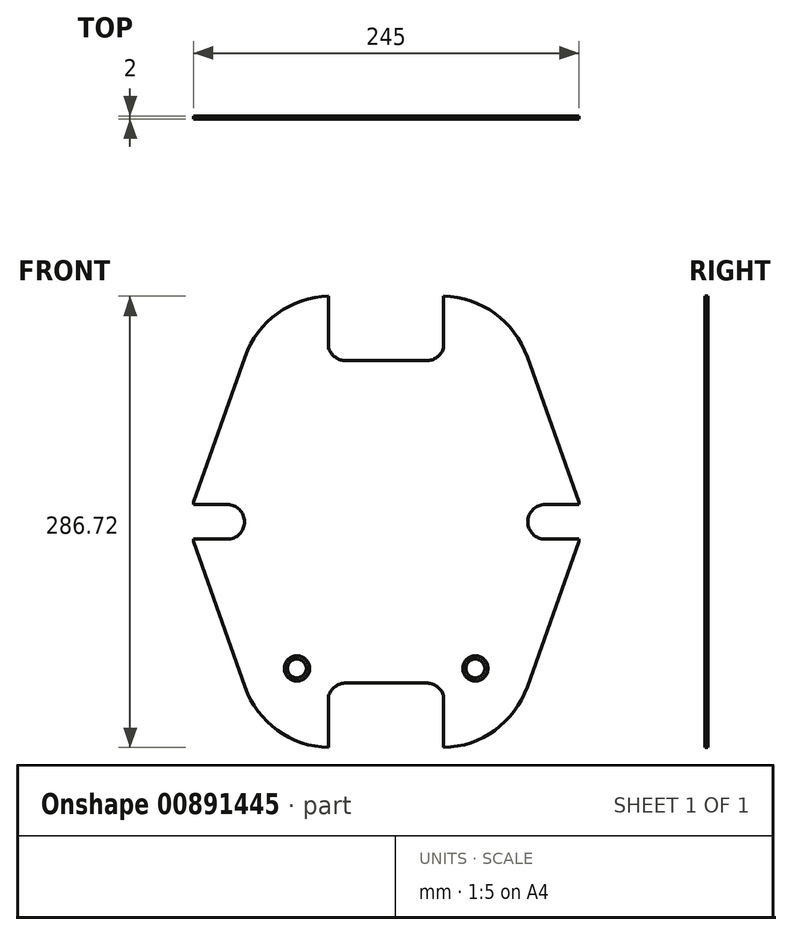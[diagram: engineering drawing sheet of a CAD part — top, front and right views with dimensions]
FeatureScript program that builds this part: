
annotation { "Feature Type Name" : "Feature", "Feature Type Description" : "" }
export const myFeature = defineFeature(function(context is Context, id is Id, definition is map)
    precondition{}
    {
        {
            var Q0;
            Q0=qCreatedBy(makeId("Front.planeOp"),FACE);
            var sketch = newSketch(context, id + "F0", { "sketchPlane" : qUnion([Q0])});
            skLineSegment(sketch, "E0", {"start": v(-122.5, 130.86) * mm, "end": v(122.5, 130.86) * mm});
            skLineSegment(sketch, "E1", {"start": v(122.5, 130.86) * mm, "end": v(89.64, 38.53) * mm});
            skLineSegment(sketch, "E2", {"start": v(-122.5, 130.86) * mm, "end": v(-89.64, 38.53) * mm});
            skArc(sketch, "E3", {"start": v(-89.64, 38.53) * mm, "mid": v(-69.05, 11.03) * mm, "end": v(-36.5, 0) * mm});
            skArc(sketch, "E4", {"start": v(36.5, 0) * mm, "mid": v(69.05, 11.03) * mm, "end": v(89.64, 38.53) * mm});
            skLineSegment(sketch, "E5", {"start": v(-36.5, 0) * mm, "end": v(-36.5, 33) * mm});
            skLineSegment(sketch, "E6", {"start": v(-36.5, 33) * mm, "end": v(36.5, 33) * mm, "construction": true});
            skLineSegment(sketch, "E7", {"start": v(36.5, 33) * mm, "end": v(36.5, 0) * mm});
            skLineSegment(sketch, "E8", {"start": v(0, 33) * mm, "end": v(0, 0) * mm, "construction": true});
            skLineSegment(sketch, "E9", {"start": v(-25.5, 41) * mm, "end": v(25.5, 41) * mm});
            skArc(sketch, "E10", {"start": v(-25.5, 41) * mm, "mid": v(-32.3, 38.79) * mm, "end": v(-36.5, 33) * mm});
            skArc(sketch, "E11", {"start": v(36.5, 33) * mm, "mid": v(32.3, 38.79) * mm, "end": v(25.5, 41) * mm});
            skPoint(sketch, "E12", {"position": v(-56.67, 50.27) * mm});
            skLineSegment(sketch, "E13", {"start": v(-89.64, 38.53) * mm, "end": v(-56.67, 50.27) * mm, "construction": true});
            skPoint(sketch, "E14", {"position": v(56.67, 50.27) * mm});
            skSolve(sketch);
        }
        {
            var Q0;
            Q0=qSketchRegion(id+"F0",true);
            extrude(context, id + "F1", {"entities" : qUnion([Q0]), "oppositeDirection" : true, "depth" : 2 * mm, "offsetDistance" : 25 * mm});
        }
        {
            var Q0;
            Q0=makeQuery(id+"F1.opExtrude","SWEPT_FACE",FACE,{"disambiguationData":[OSD([sQuery(id+"F0.wireOp",EDGE,"E0")])]});
            cPlane(context, id + "F2", {"entities" : qUnion([Q0]), "cplaneType" : CPlaneType.OFFSET, "offset" : 12.5 * mm, "width" : 150 * mm, "height" : 150 * mm});
        }
        {
            var Q0;
            Q0=makeQuery(id+"F1.opExtrude","SWEPT_BODY",BODY,{"disambiguationData":[OSD([sQuery(id+"F0.wireOp",EDGE,"E0"),sQuery(id+"F0.wireOp",EDGE,"E1"),sQuery(id+"F0.wireOp",EDGE,"E2"),sQuery(id+"F0.wireOp",EDGE,"E3"),sQuery(id+"F0.wireOp",EDGE,"RBLw4Hvx-HNYR-cSoG-CBft-1KmUEeb84xH9"),sQuery(id+"F0.wireOp",EDGE,"E4")])]});
            var Q1;
            Q1=qCreatedBy(id+"F2.planeOp",FACE);
            mirror(context, id + "F3", {"entities" : qUnion([Q0]), "mirrorPlane" : qUnion([Q1])});
        }
        {
            var Q0;
            Q0=makeQuery(id+"F1.opExtrude","CAP_FACE",FACE,{"disambiguationData":[OSD([sQuery(id+"F0.wireOp",EDGE,"E0"),sQuery(id+"F0.wireOp",EDGE,"E1"),sQuery(id+"F0.wireOp",EDGE,"E2"),sQuery(id+"F0.wireOp",EDGE,"E3"),sQuery(id+"F0.wireOp",EDGE,"RBLw4Hvx-HNYR-cSoG-CBft-1KmUEeb84xH9"),sQuery(id+"F0.wireOp",EDGE,"E4")])],"isStart":true});
            var sketch = newSketch(context, id + "F4", { "sketchPlane" : qUnion([Q0])});
            skArc(sketch, "E15", {"start": v(-101, 132.36) * mm, "mid": v(-90, 143.36) * mm, "end": v(-101, 154.36) * mm});
            skArc(sketch, "E16", {"start": v(101, 154.36) * mm, "mid": v(90, 143.36) * mm, "end": v(101, 132.36) * mm});
            skLineSegment(sketch, "E17", {"start": v(-101, 143.36) * mm, "end": v(101, 143.36) * mm, "construction": true});
            skLineSegment(sketch, "E18", {"start": v(0, 130.86) * mm, "end": v(0, 155.86) * mm, "construction": true});
            skLineSegment(sketch, "E19", {"start": v(-101, 154.36) * mm, "end": v(-122.5, 154.36) * mm});
            skLineSegment(sketch, "E20", {"start": v(-101, 132.36) * mm, "end": v(-122.5, 132.36) * mm});
            skLineSegment(sketch, "E21.0", {"start": v(-122.5, 155.86) * mm, "end": v(122.5, 155.86) * mm});
            skLineSegment(sketch, "E21.1", {"start": v(-122.5, 130.86) * mm, "end": v(122.5, 130.86) * mm});
            skLineSegment(sketch, "E22", {"start": v(-122.5, 155.86) * mm, "end": v(-122.5, 154.36) * mm});
            skLineSegment(sketch, "E23", {"start": v(-122.5, 132.36) * mm, "end": v(-122.5, 130.86) * mm});
            skLineSegment(sketch, "E24", {"start": v(101, 154.36) * mm, "end": v(122.5, 154.36) * mm});
            skLineSegment(sketch, "E25", {"start": v(101, 132.36) * mm, "end": v(122.5, 132.36) * mm});
            skLineSegment(sketch, "E26", {"start": v(122.5, 154.36) * mm, "end": v(122.5, 155.86) * mm});
            skLineSegment(sketch, "E27", {"start": v(122.5, 132.36) * mm, "end": v(122.5, 130.86) * mm});
            skSolve(sketch);
        }
        {
            var Q0;
            Q0=qSketchRegion(id+"F4",true);
            extrude(context, id + "F5", {"entities" : qUnion([Q0]), "operationType" : NewBodyOperationType.ADD, "oppositeDirection" : true, "depth" : 2 * mm, "offsetDistance" : 25 * mm});
        }
        {
            var Q0;
            Q0=sQuery(id+"F0.wireOp",VERTEX,"E12");
            var Q1;
            Q1=sQuery(id+"F0.wireOp",VERTEX,"E14");
            var Q2;
            Q2=makeQuery(id+"F1.opExtrude","SWEPT_BODY",BODY,{"disambiguationData":[OSD([sQuery(id+"F0.wireOp",EDGE,"E0"),sQuery(id+"F0.wireOp",EDGE,"E1"),sQuery(id+"F0.wireOp",EDGE,"E2"),sQuery(id+"F0.wireOp",EDGE,"E3"),sQuery(id+"F0.wireOp",EDGE,"E4"),sQuery(id+"F0.wireOp",EDGE,"E5"),sQuery(id+"F0.wireOp",EDGE,"E7"),sQuery(id+"F0.wireOp",EDGE,"E9"),sQuery(id+"F0.wireOp",EDGE,"E10"),sQuery(id+"F0.wireOp",EDGE,"E11")])]});
            hole(context, id + "F6", {"style" : HoleStyle.C_SINK, "endStyle" : HoleEndStyle.THROUGH, "holeDiameter" : 8 * mm, "cSinkDiameter" : 16 * mm, "cSinkAngle" : 90 * degree, "majorDiameter" : 5 * mm, "isTappedThrough" : true, "tappedDepth" : 12 * mm, "tapClearance" : 3, "locations" : qUnion([Q0, Q1]), "scope" : qUnion([Q2])});
        }
    });
